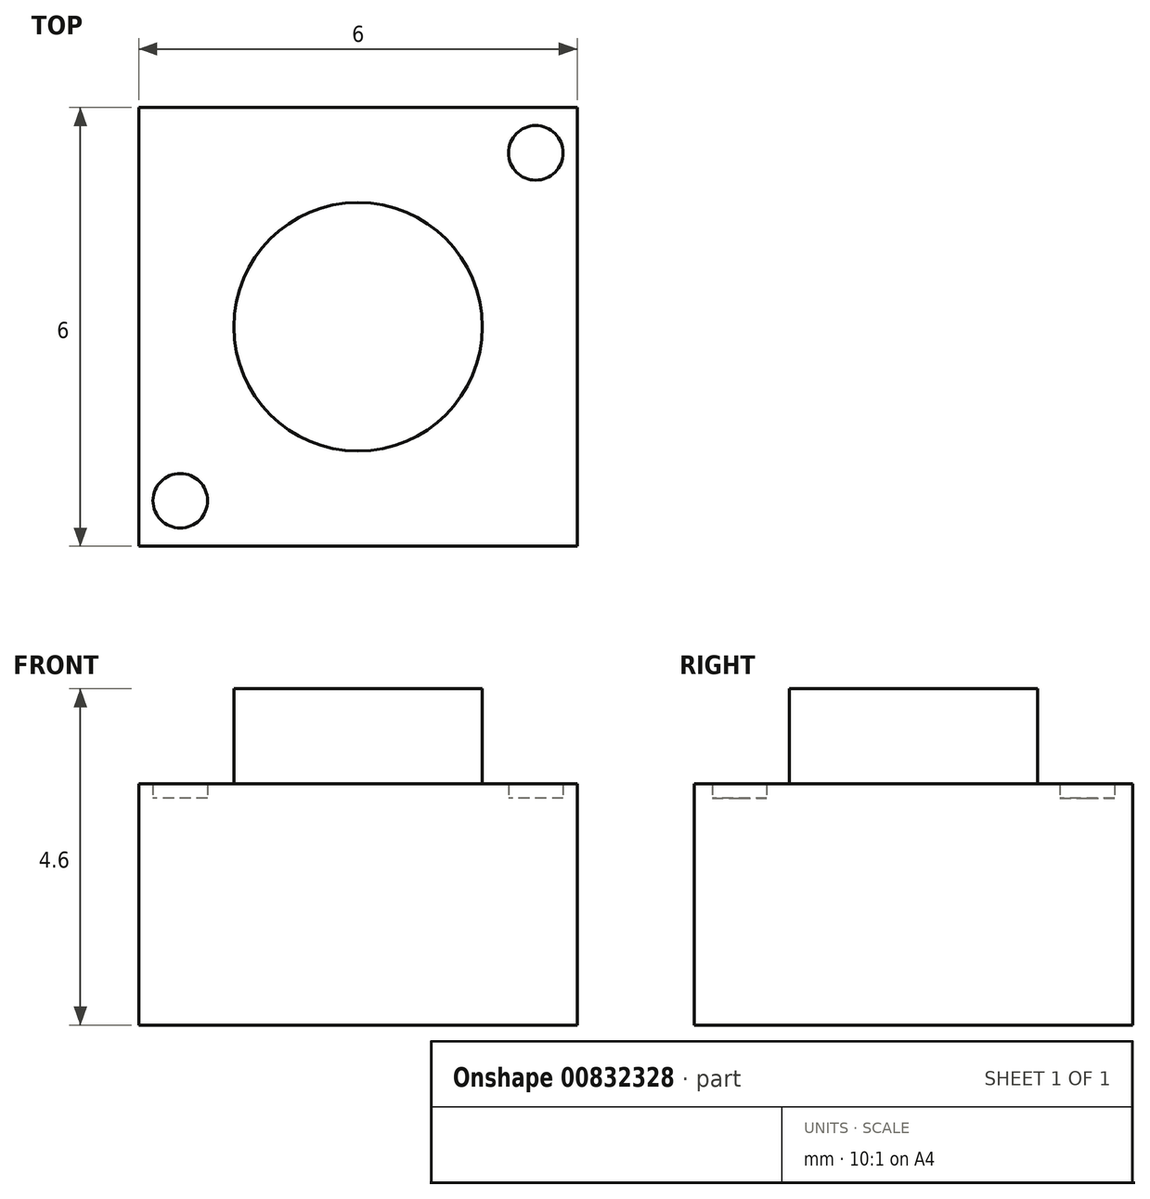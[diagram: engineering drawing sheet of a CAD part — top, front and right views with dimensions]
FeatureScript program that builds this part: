
annotation { "Feature Type Name" : "Feature", "Feature Type Description" : "" }
export const myFeature = defineFeature(function(context is Context, id is Id, definition is map)
    precondition{}
    {
        {
            var Q0;
            Q0=qCreatedBy(makeId("Top.planeOp"),FACE);
            var sketch = newSketch(context, id + "F0", { "sketchPlane" : qUnion([Q0])});
            skLineSegment(sketch, "E0.bottom", {"start": v(3, 3) * mm, "end": v(-3, 3) * mm});
            skLineSegment(sketch, "E0.top", {"start": v(3, -3) * mm, "end": v(-3, -3) * mm});
            skLineSegment(sketch, "E0.left", {"start": v(3, 3) * mm, "end": v(3, -3) * mm});
            skLineSegment(sketch, "E0.right", {"start": v(-3, 3) * mm, "end": v(-3, -3) * mm});
            skPoint(sketch, "E0.middle", {"position": v(0, 0) * mm});
            skSolve(sketch);
        }
        {
            var Q0;
            Q0=makeQuery(id+"F0.imprint","IMPRINT",FACE,{"disambiguationData":[TD([[makeQuery(id+"F0.imprint","IMPRINT",EDGE,{"derivedFrom":sQuery(id+"F0.wireOp",EDGE,"E0.bottom")}),1.0]])]});
            extrude(context, id + "F1", {"entities" : qUnion([Q0]), "depth" : 3 * mm, "offsetDistance" : 25 * mm});
        }
        {
            var Q0;
            Q0=makeQuery(id+"F1.opExtrude","CAP_FACE",FACE,{"disambiguationData":[OSD([sQuery(id+"F0.wireOp",EDGE,"E0.bottom"),sQuery(id+"F0.wireOp",EDGE,"E0.top"),sQuery(id+"F0.wireOp",EDGE,"E0.left"),sQuery(id+"F0.wireOp",EDGE,"E0.right")])],"isStart":false});
            var sketch = newSketch(context, id + "F2", { "sketchPlane" : qUnion([Q0])});
            skCircle(sketch, "E1", {"center": v(0, 0) * mm, "radius": 1.7 * mm});
            skCircle(sketch, "E2", {"center": v(-2.43, 2.38) * mm, "radius": 0.37 * mm});
            skCircle(sketch, "E3.MirrorC", {"center": v(2.43, 2.38) * mm, "radius": 0.37 * mm});
            skCircle(sketch, "E4.MirrorC", {"center": v(-2.43, -2.38) * mm, "radius": 0.37 * mm});
            skCircle(sketch, "E5.MirrorC", {"center": v(2.43, -2.38) * mm, "radius": 0.37 * mm});
            skSolve(sketch);
        }
        {
            var Q0;
            Q0=makeQuery(id+"F2.imprint","IMPRINT",FACE,{"disambiguationData":[TD([[makeQuery(id+"F2.imprint","IMPRINT",EDGE,{"derivedFrom":sQuery(id+"F2.wireOp",EDGE,"E1")}),1.0]])]});
            extrude(context, id + "F3", {"entities" : qUnion([Q0]), "depth" : 1.6 * mm, "offsetDistance" : 25 * mm});
        }
        {
            var Q0;
            Q0=makeQuery(id+"F1.opExtrude","CAP_FACE",FACE,{"disambiguationData":[OSD([sQuery(id+"F0.wireOp",EDGE,"E0.bottom"),sQuery(id+"F0.wireOp",EDGE,"E0.top"),sQuery(id+"F0.wireOp",EDGE,"E0.left"),sQuery(id+"F0.wireOp",EDGE,"E0.right")])],"isStart":false});
            extrude(context, id + "F4", {"entities" : qUnion([Q0]), "depth" : 0.1 * mm, "offsetDistance" : 25 * mm});
        }
        {
            var Q0;
            Q0=makeQuery(id+"F2.imprint","IMPRINT",FACE,{"disambiguationData":[TD([[makeQuery(id+"F2.imprint","IMPRINT",EDGE,{"derivedFrom":sQuery(id+"F2.wireOp",EDGE,"E4.MirrorC")}),-1.0]])]});
            var Q1;
            Q1=makeQuery(id+"F2.imprint","IMPRINT",FACE,{"disambiguationData":[TD([[makeQuery(id+"F2.imprint","IMPRINT",EDGE,{"derivedFrom":sQuery(id+"F2.wireOp",EDGE,"E5.MirrorC")}),1.0]])]});
            var Q2;
            Q2=makeQuery(id+"F2.imprint","IMPRINT",FACE,{"disambiguationData":[TD([[makeQuery(id+"F2.imprint","IMPRINT",EDGE,{"derivedFrom":sQuery(id+"F2.wireOp",EDGE,"E3.MirrorC")}),-1.0]])]});
            var Q3;
            Q3=makeQuery(id+"F2.imprint","IMPRINT",FACE,{"disambiguationData":[TD([[makeQuery(id+"F2.imprint","IMPRINT",EDGE,{"derivedFrom":sQuery(id+"F2.wireOp",EDGE,"E2")}),1.0]])]});
            extrude(context, id + "F5", {"entities" : qUnion([Q0, Q1, Q2, Q3]), "operationType" : NewBodyOperationType.ADD, "depth" : .3 * mm, "offsetDistance" : 25 * mm});
        }
    });
